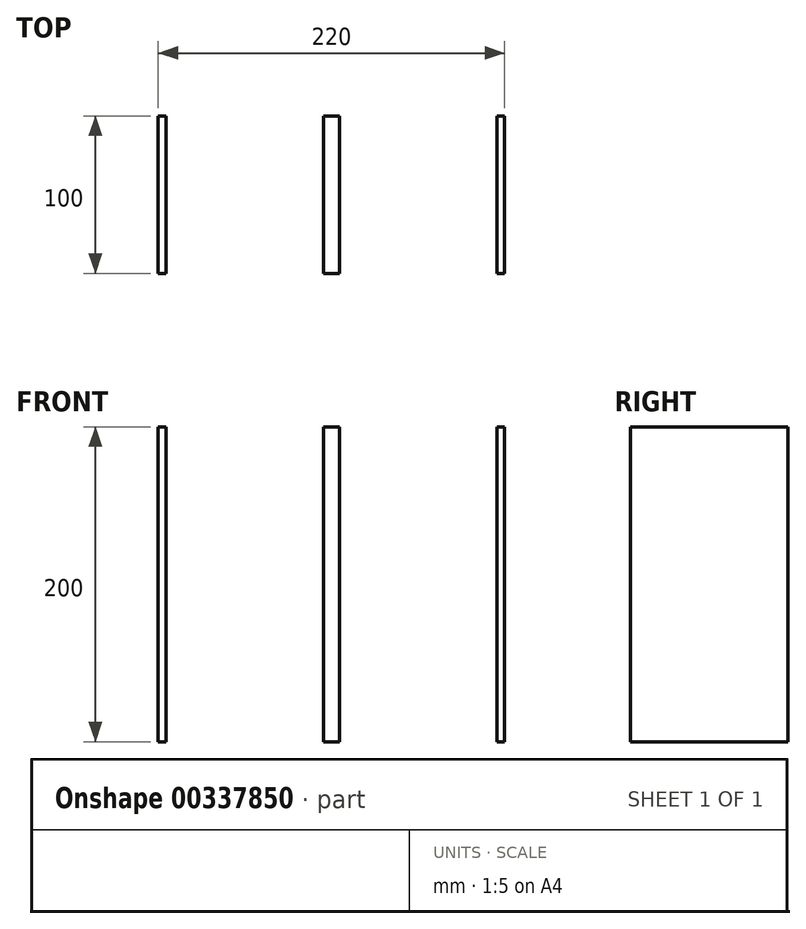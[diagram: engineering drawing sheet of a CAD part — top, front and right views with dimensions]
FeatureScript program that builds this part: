
annotation { "Feature Type Name" : "Feature", "Feature Type Description" : "" }
export const myFeature = defineFeature(function(context is Context, id is Id, definition is map)
    precondition{}
    {
        {
            var Q0;
            Q0=qCreatedBy(makeId("Front.planeOp"),FACE);
            var sketch = newSketch(context, id + "F0", { "sketchPlane" : qUnion([Q0])});
            skLineSegment(sketch, "E0", {"start": v(0, 0) * mm, "end": v(0, 100) * mm});
            skLineSegment(sketch, "E1", {"start": v(0, 100) * mm, "end": v(5, 100) * mm});
            skLineSegment(sketch, "E2", {"start": v(5, 100) * mm, "end": v(5, 0) * mm});
            skLineSegment(sketch, "E3", {"start": v(-5, 0) * mm, "end": v(-5, 100) * mm});
            skLineSegment(sketch, "E4", {"start": v(-5, 100) * mm, "end": v(0, 100) * mm});
            skLineSegment(sketch, "E5", {"start": v(5, 0) * mm, "end": v(5, -100) * mm});
            skLineSegment(sketch, "E6", {"start": v(5, -100) * mm, "end": v(0, -100) * mm});
            skLineSegment(sketch, "E7", {"start": v(0, -100) * mm, "end": v(0, 0) * mm});
            skLineSegment(sketch, "E8", {"start": v(0, -100) * mm, "end": v(-5, -100) * mm});
            skLineSegment(sketch, "E9", {"start": v(-5, -100) * mm, "end": v(-5, 0) * mm});
            skLineSegment(sketch, "E10", {"start": v(5, -100) * mm, "end": v(105, -100) * mm});
            skLineSegment(sketch, "E11", {"start": v(-5, -100) * mm, "end": v(-105, -100) * mm});
            skLineSegment(sketch, "E12", {"start": v(105, -100) * mm, "end": v(105, 100) * mm});
            skLineSegment(sketch, "E13", {"start": v(105, 100) * mm, "end": v(110, 100) * mm});
            skLineSegment(sketch, "E14", {"start": v(110, 100) * mm, "end": v(110, -100) * mm});
            skLineSegment(sketch, "E15", {"start": v(110, -100) * mm, "end": v(105, -100) * mm});
            skLineSegment(sketch, "E16", {"start": v(-105, -100) * mm, "end": v(-105, 100) * mm});
            skLineSegment(sketch, "E17", {"start": v(-105, 100) * mm, "end": v(-110, 100) * mm});
            skLineSegment(sketch, "E18", {"start": v(-110, 100) * mm, "end": v(-110, -100) * mm});
            skLineSegment(sketch, "E19", {"start": v(-110, -100) * mm, "end": v(-105, -100) * mm});
            skSolve(sketch);
        }
        {
            var Q0;
            Q0=makeQuery(id+"F0.imprint","IMPRINT",FACE,{"disambiguationData":[TD([[makeQuery(id+"F0.imprint","IMPRINT",EDGE,{"derivedFrom":sQuery(id+"F0.wireOp",EDGE,"E0")}),-1.0]])]});
            var Q1;
            Q1=makeQuery(id+"F0.imprint","IMPRINT",FACE,{"disambiguationData":[TD([[makeQuery(id+"F0.imprint","IMPRINT",EDGE,{"derivedFrom":sQuery(id+"F0.wireOp",EDGE,"E0")}),1.0]])]});
            var Q2;
            Q2=makeQuery(id+"F0.imprint","IMPRINT",FACE,{"disambiguationData":[TD([[makeQuery(id+"F0.imprint","IMPRINT",EDGE,{"derivedFrom":sQuery(id+"F0.wireOp",EDGE,"E12")}),-1.0]])]});
            var Q3;
            Q3=makeQuery(id+"F0.imprint","IMPRINT",FACE,{"disambiguationData":[TD([[makeQuery(id+"F0.imprint","IMPRINT",EDGE,{"derivedFrom":sQuery(id+"F0.wireOp",EDGE,"E16")}),1.0]])]});
            extrude(context, id + "F1", {"entities" : qUnion([Q0, Q1, Q2, Q3]), "depth" : 100 * mm});
        }
    });
